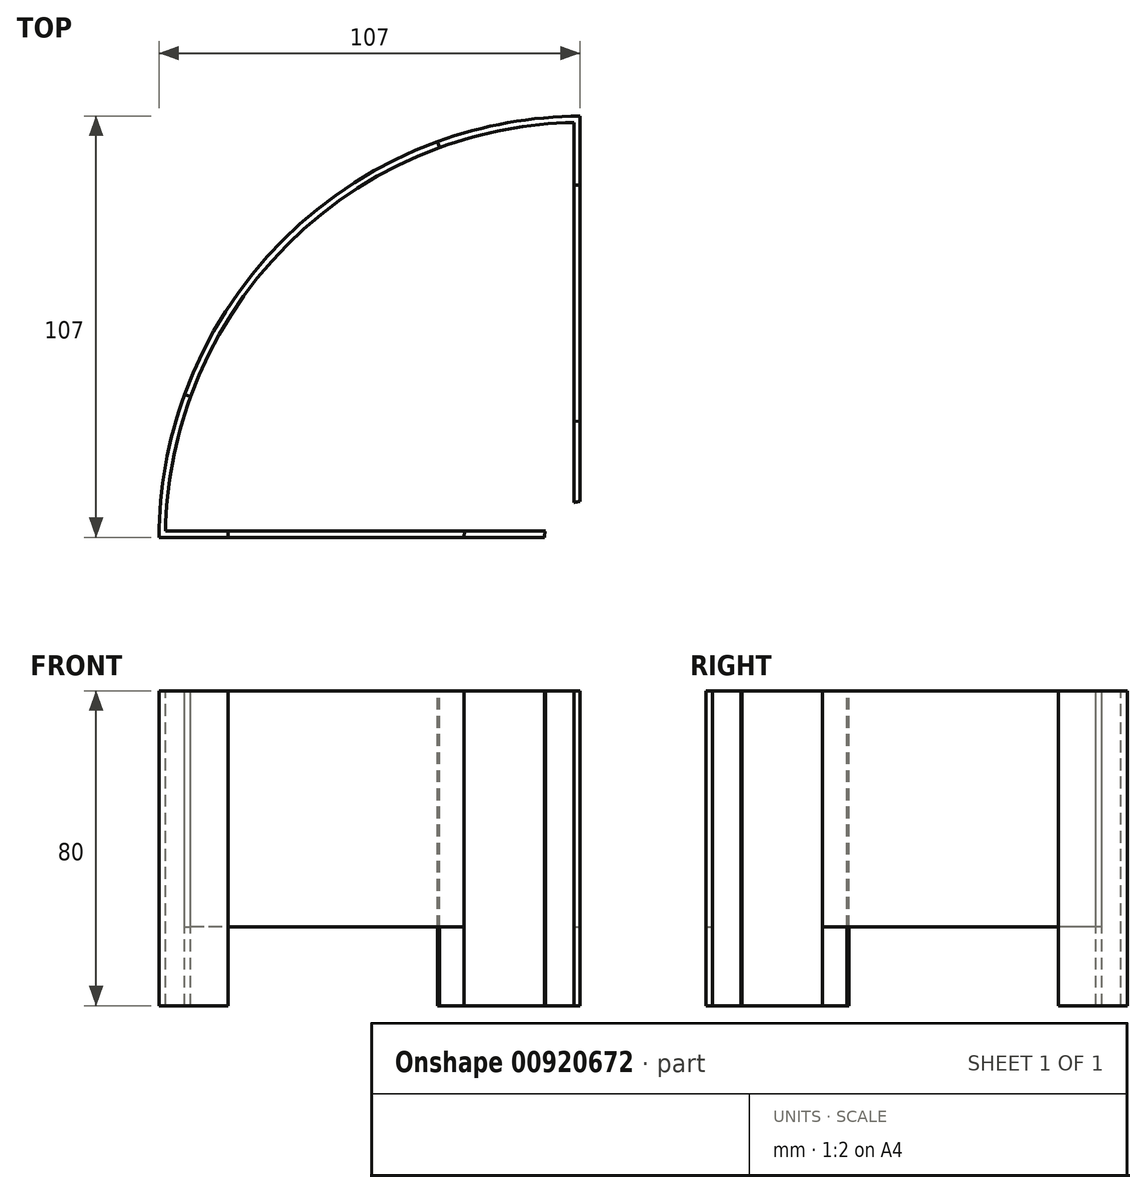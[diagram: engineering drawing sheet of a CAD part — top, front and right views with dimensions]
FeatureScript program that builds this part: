
annotation { "Feature Type Name" : "Feature", "Feature Type Description" : "" }
export const myFeature = defineFeature(function(context is Context, id is Id, definition is map)
    precondition{}
    {
        {
            var Q0;
            Q0=qCreatedBy(makeId("Top.planeOp"),FACE);
            var sketch = newSketch(context, id + "F0", { "sketchPlane" : qUnion([Q0])});
            skCircle(sketch, "E0", {"center": v(0, 0) * mm, "radius": 8 * mm});
            skLineSegment(sketch, "E1", {"start": v(0, 0) * mm, "end": v(-131.48, 0) * mm, "construction": true});
            skLineSegment(sketch, "E2", {"start": v(0, 0) * mm, "end": v(0, 113.56) * mm, "construction": true});
            skArc(sketch, "E3", {"start": v(-0.5, 107.5) * mm, "mid": v(-76.01, 76.01) * mm, "end": v(-107.5, 0.5) * mm});
            skLineSegment(sketch, "E4", {"start": v(-0.5, 7.98) * mm, "end": v(-0.5, 107.5) * mm});
            skLineSegment(sketch, "E5", {"start": v(-7.98, 0.5) * mm, "end": v(-107.5, 0.5) * mm});
            skLineSegment(sketch, "E6", {"start": v(-107.5, 0.5) * mm, "end": v(-107.5, 0.5) * mm});
            skLineSegment(sketch, "E7", {"start": v(-7.98, 0.5) * mm, "end": v(-7.98, 0.5) * mm});
            skLineSegment(sketch, "E8.0", {"start": v(-7.98, 2.1) * mm, "end": v(-105.88, 2.1) * mm});
            skArc(sketch, "E8.1", {"start": v(-2.1, 105.88) * mm, "mid": v(-74.88, 74.88) * mm, "end": v(-105.88, 2.1) * mm});
            skLineSegment(sketch, "E8.2", {"start": v(-2.1, 7.98) * mm, "end": v(-2.1, 105.88) * mm});
            skCircle(sketch, "E9.0", {"center": v(0, 0) * mm, "radius": 9.6 * mm});
            skCircle(sketch, "E10", {"center": v(0, 0) * mm, "radius": 90 * mm, "construction": true});
            skCircle(sketch, "E11", {"center": v(0, 0) * mm, "radius": 30 * mm, "construction": true});
            skLineSegment(sketch, "E12", {"start": v(0, 0) * mm, "end": v(-130.44, 47.48) * mm, "construction": true});
            skLineSegment(sketch, "E13", {"start": v(0, 0) * mm, "end": v(-81.48, 29.66) * mm});
            skLineSegment(sketch, "E14", {"start": v(0, 0) * mm, "end": v(-47.48, 130.44) * mm, "construction": true});
            skLineSegment(sketch, "E15", {"start": v(-101.02, 36.77) * mm, "end": v(-99.51, 36.22) * mm});
            skLineSegment(sketch, "E16", {"start": v(-90, 0.5) * mm, "end": v(-89.98, 2.11) * mm});
            skLineSegment(sketch, "E17", {"start": v(-30, 0.5) * mm, "end": v(-29.93, 2.1) * mm});
            skLineSegment(sketch, "E18", {"start": v(-2.1, 29.93) * mm, "end": v(-0.5, 30.04) * mm});
            skLineSegment(sketch, "E19", {"start": v(-2.1, 89.98) * mm, "end": v(-0.5, 90.01) * mm});
            skLineSegment(sketch, "E20", {"start": v(-36.77, 101.02) * mm, "end": v(-36.22, 99.51) * mm});
            skSolve(sketch);
        }
        {
            var Q0;
            {var subQ3=sQuery(id+"F0.wireOp",EDGE,"E19");Q0=makeQuery(id+"F0.imprint","IMPRINT",FACE,{"disambiguationData":[TD([[makeQuery(id+"F0.imprint","IMPRINT",EDGE,{"derivedFrom":subQ3}),1.0]])]});}
            var Q1;
            {var subQ0=sQuery(id+"F0.wireOp",EDGE,"E18");Q1=makeQuery(id+"F0.imprint","IMPRINT",FACE,{"disambiguationData":[TD([[makeQuery(id+"F0.imprint","IMPRINT",EDGE,{"derivedFrom":subQ0}),-1.0]])]});}
            var Q2;
            {var subQ0=sQuery(id+"F0.wireOp",EDGE,"E17");Q2=makeQuery(id+"F0.imprint","IMPRINT",FACE,{"disambiguationData":[TD([[makeQuery(id+"F0.imprint","IMPRINT",EDGE,{"derivedFrom":subQ0}),-1.0]])]});}
            var Q3;
            {var subQ3=sQuery(id+"F0.wireOp",EDGE,"E15");Q3=makeQuery(id+"F0.imprint","IMPRINT",FACE,{"disambiguationData":[TD([[makeQuery(id+"F0.imprint","IMPRINT",EDGE,{"derivedFrom":subQ3}),-1.0]])]});}
            extrude(context, id + "F1", {"entities" : qUnion([Q0, Q1, Q2, Q3]), "oppositeDirection" : true, "depth" : 80 * mm, "offsetDistance" : 25 * mm});
        }
        {
            var Q0;
            {var subQ3=sQuery(id+"F0.wireOp",EDGE,"E17");Q0=makeQuery(id+"F0.imprint","IMPRINT",FACE,{"disambiguationData":[TD([[makeQuery(id+"F0.imprint","IMPRINT",EDGE,{"derivedFrom":subQ3}),1.0]])]});}
            var Q1;
            {var subQ0=sQuery(id+"F0.wireOp",EDGE,"E18");Q1=makeQuery(id+"F0.imprint","IMPRINT",FACE,{"disambiguationData":[TD([[makeQuery(id+"F0.imprint","IMPRINT",EDGE,{"derivedFrom":subQ0}),1.0]])]});}
            var Q2;
            {var subQ0=sQuery(id+"F0.wireOp",EDGE,"E15");Q2=makeQuery(id+"F0.imprint","IMPRINT",FACE,{"disambiguationData":[TD([[makeQuery(id+"F0.imprint","IMPRINT",EDGE,{"derivedFrom":subQ0}),1.0]])]});}
            extrude(context, id + "F2", {"entities" : qUnion([Q0, Q1, Q2]), "oppositeDirection" : true, "depth" : 60 * mm, "offsetDistance" : 25 * mm});
        }
    });
